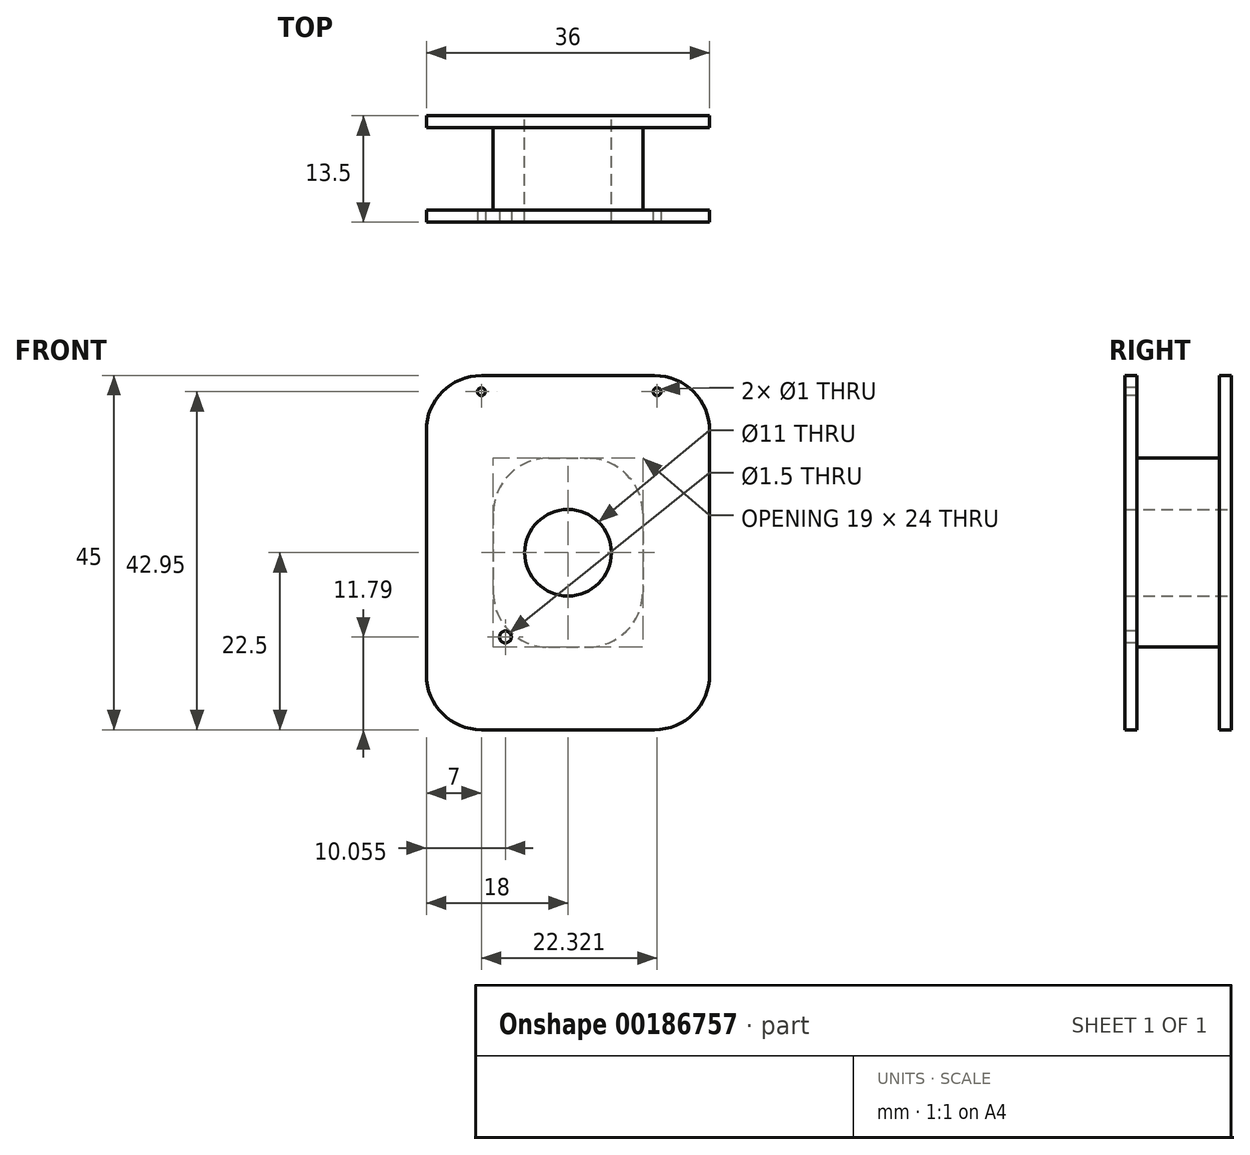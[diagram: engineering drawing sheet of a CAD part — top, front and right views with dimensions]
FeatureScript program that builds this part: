
annotation { "Feature Type Name" : "Feature", "Feature Type Description" : "" }
export const myFeature = defineFeature(function(context is Context, id is Id, definition is map)
    precondition{}
    {
        {
            var Q0;
            Q0=qCreatedBy(makeId("Front.planeOp"),FACE);
            var sketch = newSketch(context, id + "F0", { "sketchPlane" : qUnion([Q0])});
            skLineSegment(sketch, "E0.bottom", {"start": v(-18, 22.5) * mm, "end": v(18, 22.5) * mm});
            skLineSegment(sketch, "E0.top", {"start": v(-18, -22.5) * mm, "end": v(18, -22.5) * mm});
            skLineSegment(sketch, "E0.left", {"start": v(-18, 22.5) * mm, "end": v(-18, -22.5) * mm});
            skLineSegment(sketch, "E0.right", {"start": v(18, 22.5) * mm, "end": v(18, -22.5) * mm});
            skPoint(sketch, "E0.middle", {"position": v(0, 0) * mm});
            skCircle(sketch, "E1", {"center": v(0, 0) * mm, "radius": 5.5 * mm});
            skSolve(sketch);
        }
        {
            var Q0;
            Q0=makeQuery(id+"F0.imprint","IMPRINT",FACE,{"disambiguationData":[TD([[makeQuery(id+"F0.imprint","IMPRINT",EDGE,{"derivedFrom":sQuery(id+"F0.wireOp",EDGE,"E0.bottom")}),-1.0]])]});
            var Q1;
            Q1=makeQuery(id+"F0.imprint","IMPRINT",FACE,{"disambiguationData":[TD([[makeQuery(id+"F0.imprint","IMPRINT",EDGE,{"derivedFrom":sQuery(id+"F0.wireOp",EDGE,"K3YnusOH-pDpb-mAzx-DvoV-s8gcL6kEX4wQ.bottom")}),-1.0]])]});
            extrude(context, id + "F1", {"entities" : qUnion([Q0, Q1]), "depth" : 1.5 * mm});
        }
        {
            var Q0;
            Q0=makeQuery(id+"F1.opExtrude","CAP_FACE",FACE,{"disambiguationData":[OSD([sQuery(id+"F0.wireOp",EDGE,"E0.bottom"),sQuery(id+"F0.wireOp",EDGE,"E0.top"),sQuery(id+"F0.wireOp",EDGE,"E0.left"),sQuery(id+"F0.wireOp",EDGE,"E0.right"),sQuery(id+"F0.wireOp",EDGE,"E1")])],"isStart":false});
            var sketch = newSketch(context, id + "F2", { "sketchPlane" : qUnion([Q0])});
            skLineSegment(sketch, "E2.bottom", {"start": v(-9.5, 12) * mm, "end": v(9.5, 12) * mm});
            skLineSegment(sketch, "E2.top", {"start": v(-9.5, -12) * mm, "end": v(9.5, -12) * mm});
            skLineSegment(sketch, "E2.left", {"start": v(-9.5, 12) * mm, "end": v(-9.5, -12) * mm});
            skLineSegment(sketch, "E2.right", {"start": v(9.5, 12) * mm, "end": v(9.5, -12) * mm});
            skPoint(sketch, "E2.middle", {"position": v(0, 0) * mm});
            skSolve(sketch);
        }
        {
            var Q0;
            Q0=makeQuery(id+"F2.imprint","IMPRINT",FACE,{"disambiguationData":[TD([[makeQuery(id+"F2.imprint","IMPRINT",EDGE,{"derivedFrom":sQuery(id+"F2.wireOp",EDGE,"E2.bottom")}),-1.0]])]});
            extrude(context, id + "F3", {"entities" : qUnion([Q0]), "operationType" : NewBodyOperationType.ADD, "depth" : 12 * mm});
        }
        {
            var Q0;
            Q0=makeQuery(id+"F3.opExtrude","CAP_FACE",FACE,{"disambiguationData":[OSD([sQuery(id+"F0.wireOp",EDGE,"E1"),sQuery(id+"F2.wireOp",EDGE,"E2.bottom"),sQuery(id+"F2.wireOp",EDGE,"E2.top"),sQuery(id+"F2.wireOp",EDGE,"E2.left"),sQuery(id+"F2.wireOp",EDGE,"E2.right")])],"isStart":false});
            var sketch = newSketch(context, id + "F4", { "sketchPlane" : qUnion([Q0])});
            skLineSegment(sketch, "E3.bottom", {"start": v(-18, 22.5) * mm, "end": v(18, 22.5) * mm});
            skLineSegment(sketch, "E3.top", {"start": v(-18, -22.5) * mm, "end": v(18, -22.5) * mm});
            skLineSegment(sketch, "E3.left", {"start": v(-18, 22.5) * mm, "end": v(-18, -22.5) * mm});
            skLineSegment(sketch, "E3.right", {"start": v(18, 22.5) * mm, "end": v(18, -22.5) * mm});
            skPoint(sketch, "E3.middle", {"position": v(0, 0) * mm});
            skSolve(sketch);
        }
        {
            var Q0;
            Q0=makeQuery(id+"F4.imprint","IMPRINT",FACE,{"disambiguationData":[TD([[makeQuery(id+"F4.imprint","IMPRINT",EDGE,{"derivedFrom":sQuery(id+"F4.wireOp",EDGE,"E3.bottom")}),-1.0]])]});
            var Q1;
            Q1=makeQuery(id+"F4.imprint","IMPRINT",FACE,{"disambiguationData":[TD([[makeQuery(id+"F4.imprint","IMPRINT",EDGE,{"derivedFrom":makeQuery(id+"F3.opExtrude","CAP_EDGE",EDGE,{"disambiguationData":[OSD([sQuery(id+"F2.wireOp",EDGE,"E2.bottom")])],"isStart":false})}),-1.0]])]});
            extrude(context, id + "F5", {"entities" : qUnion([Q0, Q1]), "operationType" : NewBodyOperationType.ADD, "oppositeDirection" : true, "depth" : 1.5 * mm});
        }
        {
            var Q0;
            Q0=makeQuery(id+"F3.opExtrude","SWEPT_EDGE",EDGE,{"disambiguationData":[OSD([sQuery(id+"F2.wireOp",EDGE,"E2.bottom"),sQuery(id+"F2.wireOp",EDGE,"E2.right")])]});
            var Q1;
            Q1=makeQuery(id+"F3.opExtrude","SWEPT_EDGE",EDGE,{"disambiguationData":[OSD([sQuery(id+"F2.wireOp",EDGE,"E2.top"),sQuery(id+"F2.wireOp",EDGE,"E2.right")])]});
            var Q2;
            Q2=makeQuery(id+"F1.opExtrude","SWEPT_EDGE",EDGE,{"disambiguationData":[OSD([sQuery(id+"F0.wireOp",EDGE,"E0.bottom"),sQuery(id+"F0.wireOp",EDGE,"E0.right")])]});
            var Q3;
            Q3=makeQuery(id+"F5.opExtrude","SWEPT_EDGE",EDGE,{"disambiguationData":[OSD([sQuery(id+"F4.wireOp",EDGE,"E3.bottom"),sQuery(id+"F4.wireOp",EDGE,"E3.right")])]});
            var Q4;
            Q4=makeQuery(id+"F5.opExtrude","SWEPT_EDGE",EDGE,{"disambiguationData":[OSD([sQuery(id+"F4.wireOp",EDGE,"E3.top"),sQuery(id+"F4.wireOp",EDGE,"E3.right")])]});
            var Q5;
            Q5=makeQuery(id+"F1.opExtrude","SWEPT_EDGE",EDGE,{"disambiguationData":[OSD([sQuery(id+"F0.wireOp",EDGE,"E0.top"),sQuery(id+"F0.wireOp",EDGE,"E0.right")])]});
            var Q6;
            Q6=makeQuery(id+"F1.opExtrude","SWEPT_EDGE",EDGE,{"disambiguationData":[OSD([sQuery(id+"F0.wireOp",EDGE,"E0.top"),sQuery(id+"F0.wireOp",EDGE,"E0.left")])]});
            var Q7;
            Q7=makeQuery(id+"F5.opExtrude","SWEPT_EDGE",EDGE,{"disambiguationData":[OSD([sQuery(id+"F4.wireOp",EDGE,"E3.top"),sQuery(id+"F4.wireOp",EDGE,"E3.left")])]});
            var Q8;
            Q8=makeQuery(id+"F3.opExtrude","SWEPT_EDGE",EDGE,{"disambiguationData":[OSD([sQuery(id+"F2.wireOp",EDGE,"E2.top"),sQuery(id+"F2.wireOp",EDGE,"E2.left")])]});
            var Q9;
            Q9=makeQuery(id+"F3.opExtrude","SWEPT_EDGE",EDGE,{"disambiguationData":[OSD([sQuery(id+"F2.wireOp",EDGE,"E2.bottom"),sQuery(id+"F2.wireOp",EDGE,"E2.left")])]});
            var Q10;
            Q10=makeQuery(id+"F1.opExtrude","SWEPT_EDGE",EDGE,{"disambiguationData":[OSD([sQuery(id+"F0.wireOp",EDGE,"E0.bottom"),sQuery(id+"F0.wireOp",EDGE,"E0.left")])]});
            var Q11;
            Q11=makeQuery(id+"F5.opExtrude","SWEPT_EDGE",EDGE,{"disambiguationData":[OSD([sQuery(id+"F4.wireOp",EDGE,"E3.bottom"),sQuery(id+"F4.wireOp",EDGE,"E3.left")])]});
            fillet(context, id + "F6", {"entities" : qUnion([Q0, Q1, Q2, Q3, Q4, Q5, Q6, Q7, Q8, Q9, Q10, Q11]), "radius" : 7 * mm, "tangentPropagation" : true, "allowEdgeOverflow" : false});
        }
        {
            var Q0;
            {var subQ0=sQuery(id+"F0.wireOp",EDGE,"E1");Q0=makeQuery(id+"F5.boolean.opBoolean","MERGE",FACE,{"derivedFrom":[makeQuery(id+"F3.opExtrude","CAP_FACE",FACE,{"disambiguationData":[OSD([subQ0,sQuery(id+"F2.wireOp",EDGE,"E2.bottom"),sQuery(id+"F2.wireOp",EDGE,"E2.top"),sQuery(id+"F2.wireOp",EDGE,"E2.left"),sQuery(id+"F2.wireOp",EDGE,"E2.right")])],"isStart":false}),makeQuery(id+"F5.opExtrude","CAP_FACE",FACE,{"disambiguationData":[OSD([subQ0,sQuery(id+"F4.wireOp",EDGE,"E3.bottom"),sQuery(id+"F4.wireOp",EDGE,"E3.top"),sQuery(id+"F4.wireOp",EDGE,"E3.left"),sQuery(id+"F4.wireOp",EDGE,"E3.right")])],"isStart":true})]});}
            var sketch = newSketch(context, id + "F7", { "sketchPlane" : qUnion([Q0])});
            skCircle(sketch, "E4", {"center": v(-7.94, -10.71) * mm, "radius": 0.75 * mm});
            skPoint(sketch, "E5.middle", {"position": v(0, 0) * mm});
            skSolve(sketch);
        }
        {
            var Q0;
            Q0=makeQuery(id+"F7.imprint","IMPRINT",FACE,{"disambiguationData":[TD([[makeQuery(id+"F7.imprint","IMPRINT",EDGE,{"derivedFrom":sQuery(id+"F7.wireOp",EDGE,"E4")}),1.0]])]});
            extrude(context, id + "F8", {"entities" : qUnion([Q0]), "operationType" : NewBodyOperationType.REMOVE, "oppositeDirection" : true, "depth" : 2.5 * mm});
        }
        {
            var Q0;
            {var subQ0=sQuery(id+"F0.wireOp",EDGE,"E1");Q0=makeQuery(id+"F5.boolean.opBoolean","MERGE",FACE,{"derivedFrom":[makeQuery(id+"F3.opExtrude","CAP_FACE",FACE,{"disambiguationData":[OSD([subQ0,sQuery(id+"F2.wireOp",EDGE,"E2.bottom"),sQuery(id+"F2.wireOp",EDGE,"E2.top"),sQuery(id+"F2.wireOp",EDGE,"E2.left"),sQuery(id+"F2.wireOp",EDGE,"E2.right")])],"isStart":false}),makeQuery(id+"F5.opExtrude","CAP_FACE",FACE,{"disambiguationData":[OSD([subQ0,sQuery(id+"F4.wireOp",EDGE,"E3.bottom"),sQuery(id+"F4.wireOp",EDGE,"E3.top"),sQuery(id+"F4.wireOp",EDGE,"E3.left"),sQuery(id+"F4.wireOp",EDGE,"E3.right")])],"isStart":true})]});}
            var sketch = newSketch(context, id + "F9", { "sketchPlane" : qUnion([Q0])});
            skCircle(sketch, "E6", {"center": v(11.32, 20.45) * mm, "radius": 0.5 * mm});
            skCircle(sketch, "E7", {"center": v(-11, 20.45) * mm, "radius": 0.5 * mm});
            skSolve(sketch);
        }
        {
            var Q0;
            Q0=makeQuery(id+"F9.imprint","IMPRINT",FACE,{"disambiguationData":[TD([[makeQuery(id+"F9.imprint","IMPRINT",EDGE,{"derivedFrom":sQuery(id+"F9.wireOp",EDGE,"E7")}),1.0]])]});
            var Q1;
            Q1=makeQuery(id+"F9.imprint","IMPRINT",FACE,{"disambiguationData":[TD([[makeQuery(id+"F9.imprint","IMPRINT",EDGE,{"derivedFrom":sQuery(id+"F9.wireOp",EDGE,"E6")}),1.0]])]});
            extrude(context, id + "F10", {"entities" : qUnion([Q0, Q1]), "operationType" : NewBodyOperationType.REMOVE, "oppositeDirection" : true, "depth" : 2.5 * mm});
        }
    });
